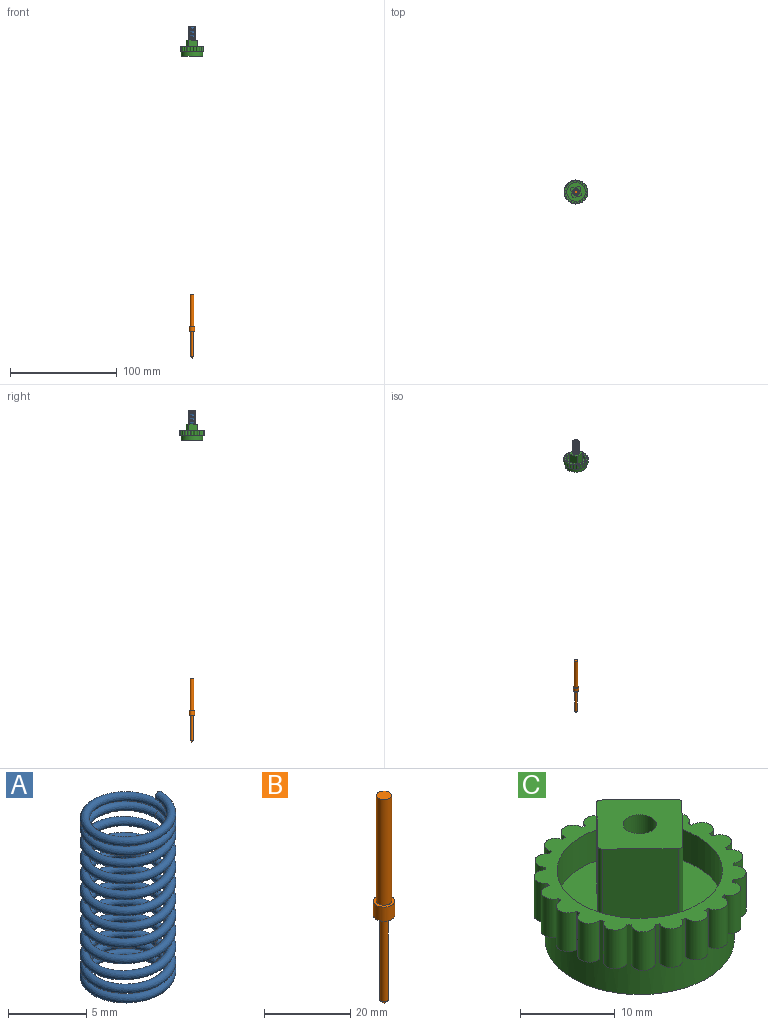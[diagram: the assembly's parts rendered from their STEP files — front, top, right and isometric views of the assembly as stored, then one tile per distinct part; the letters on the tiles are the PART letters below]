
ASSEMBLY  parts=3 mates=1
PART A: 5 faces, bbox 6.7x7.7x13.6 mm
  f0: plane 0.6x0.6mm, normal (0,1,0), area 0.3mm2, adj f1
  f1: bspline ~7.74x6.7mm, area 65.2mm2, adj f0,f2
  f2: bspline ~10.6x7.74mm, area 261.7mm2, adj f1,f4
  f3: plane 0.6x0.6mm, normal (0,-1,0), area 0.3mm2, adj f4
  f4: bspline ~7.74x6.7mm, area 65.2mm2, adj f2,f3
PART B: 7 faces, bbox 5x5x59 mm
  f0: cylinder r=2.5mm len=5mm, axis (0,0,1), area 62.8mm2, adj f3,f5
  f1: cylinder r=1mm len=24mm, axis (0,0,-1), area 150.8mm2, adj f2,f3
  f2: cone r=1mm half-angle=45deg, axis (0,0,1), area 4.4mm2, adj f1
  f3: plane 5x5mm, normal (0,0,-1), area 16.5mm2, adj f0,f1
  f4: cylinder r=1.75mm len=30mm, axis (0,0,1), area 329.9mm2, adj f5,f6
  f5: plane 5x5mm, normal (0,0,1), area 10mm2, adj f0,f4
  f6: plane 3.5x3.5mm, normal (0,0,1), area 9.6mm2, adj f4
PART C: 57 faces, bbox 22.4x22.4x15 mm
  f0: plane 17.5x17.5mm, normal (0,0,1), area 159.7mm2, adj f1,f2,f3,f4,f47,f53,f54,f55
  f1: plane 10x5.73mm, normal (0.72,-0.7,0), area 80mm2, adj f0,f5,f53,f56
  f2: plane 10x5.73mm, normal (0.7,0.72,0), area 80mm2, adj f0,f5,f53,f54
  f3: plane 10x5.73mm, normal (-0.72,0.7,0), area 80mm2, adj f0,f5,f54,f55
  f4: plane 10x5.73mm, normal (-0.7,-0.72,0), area 80mm2, adj f0,f5,f55,f56
  f5: plane 12.31x12.31mm, normal (0,0,1), area 71.2mm2, adj f1,f2,f3,f4,f52,f53,f54,f55
  f6: plane 2.44x1.78mm, normal (0,0,-1), area 2.5mm2, adj f43,f51
  f7: plane 2.27x2.09mm, normal (0,0,-1), area 2.5mm2, adj f44,f51
  f8: plane 2.32x2.02mm, normal (0,0,-1), area 2.5mm2, adj f45,f51
  f9: plane 2.47x1.69mm, normal (0,0,-1), area 2.5mm2, adj f46,f51
  f10: plane 2.5x1.33mm, normal (0,0,-1), area 2.5mm2, adj f26,f51
  f11: plane 2.47x1.69mm, normal (0,0,-1), area 2.5mm2, adj f27,f51
  f12: plane 2.32x2.02mm, normal (0,0,-1), area 2.5mm2, adj f28,f51
  f13: plane 2.27x2.09mm, normal (0,0,-1), area 2.5mm2, adj f29,f51
  f14: plane 2.44x1.78mm, normal (0,0,-1), area 2.5mm2, adj f30,f51
  f15: plane 2.5x1.42mm, normal (0,0,-1), area 2.5mm2, adj f31,f51
  f16: plane 2.48x1.6mm, normal (0,0,-1), area 2.5mm2, adj f32,f51
  f17: plane 2.37x1.94mm, normal (0,0,-1), area 2.5mm2, adj f33,f51
  f18: plane 2.22x2.16mm, normal (0,0,-1), area 2.5mm2, adj f34,f51
  f19: plane 2.41x1.86mm, normal (0,0,-1), area 2.5mm2, adj f35,f51
  f20: plane 2.5x1.51mm, normal (0,0,-1), area 2.5mm2, adj f36,f51
  f21: plane 2.5x1.51mm, normal (0,0,-1), area 2.5mm2, adj f37,f51
  f22: plane 2.41x1.86mm, normal (0,0,-1), area 2.5mm2, adj f38,f51
  f23: plane 2.22x2.16mm, normal (0,0,-1), area 2.5mm2, adj f39,f51
  f24: plane 2.37x1.94mm, normal (0,0,-1), area 2.5mm2, adj f40,f51
  f25: plane 2.48x1.6mm, normal (0,0,-1), area 2.5mm2, adj f41,f51
  f26: cylinder r=1.25mm len=5mm, axis (0,0,-1), area 20.4mm2, adj f10,f48,f51
  f27: cylinder r=1.25mm len=5mm, axis (0,0,-1), area 20.4mm2, adj f11,f48,f51
  f28: cylinder r=1.25mm len=5mm, axis (0,0,-1), area 20.4mm2, adj f12,f48,f51
  f29: cylinder r=1.25mm len=5mm, axis (0,0,-1), area 20.4mm2, adj f13,f48,f51
  f30: cylinder r=1.25mm len=5mm, axis (0,0,-1), area 20.4mm2, adj f14,f48,f51
  f31: cylinder r=1.25mm len=5mm, axis (0,0,-1), area 20.4mm2, adj f15,f48,f51
  f32: cylinder r=1.25mm len=5mm, axis (0,0,-1), area 20.4mm2, adj f16,f48,f51
  f33: cylinder r=1.25mm len=5mm, axis (0,0,-1), area 20.4mm2, adj f17,f48,f51
  f34: cylinder r=1.25mm len=5mm, axis (0,0,-1), area 20.4mm2, adj f18,f48,f51
  f35: cylinder r=1.25mm len=5mm, axis (0,0,-1), area 20.4mm2, adj f19,f48,f51
  f36: cylinder r=1.25mm len=5mm, axis (0,0,-1), area 20.4mm2, adj f20,f48,f51
  f37: cylinder r=1.25mm len=5mm, axis (0,0,-1), area 20.4mm2, adj f21,f48,f51
  f38: cylinder r=1.25mm len=5mm, axis (0,0,-1), area 20.4mm2, adj f22,f48,f51
  f39: cylinder r=1.25mm len=5mm, axis (0,0,-1), area 20.4mm2, adj f23,f48,f51
  f40: cylinder r=1.25mm len=5mm, axis (0,0,-1), area 20.4mm2, adj f24,f48,f51
  f41: cylinder r=1.25mm len=5mm, axis (0,0,-1), area 20.4mm2, adj f25,f48,f51
  f42: cylinder r=1.25mm len=5mm, axis (0,0,-1), area 20.4mm2, adj f48,f49,f51
  f43: cylinder r=1.25mm len=5mm, axis (0,0,-1), area 20.4mm2, adj f6,f48,f51
  f44: cylinder r=1.25mm len=5mm, axis (0,0,-1), area 20.4mm2, adj f7,f48,f51
  f45: cylinder r=1.25mm len=5mm, axis (0,0,-1), area 20.4mm2, adj f8,f48,f51
  f46: cylinder r=1.25mm len=5mm, axis (0,0,-1), area 20.4mm2, adj f9,f48,f51
  f47: cylinder r=8.75mm len=17.5mm, axis (0,0,-1), area 219.9mm2, adj f0,f48
  f48: plane 22.44x22.39mm, normal (0,0,1), area 126.5mm2, adj f26,f27,f28,f29,f30,f31,f32,f33
  f49: plane 2.5x1.42mm, normal (0,0,-1), area 2.5mm2, adj f42,f51
  f50: plane 20x20mm, normal (0,0,-1), area 304.5mm2, adj f51,f52
  f51: cylinder r=10mm len=20mm, axis (0,0,-1), area 302.8mm2, adj f6,f7,f8,f9,f10,f11,f12,f13
  f52: cylinder r=1.75mm len=15mm, axis (0,0,-1), area 164.9mm2, adj f5,f50
  f53: cylinder r=0.5mm len=10mm, axis (0,0,-1), area 7.9mm2, adj f0,f1,f2,f5
  f54: cylinder r=0.5mm len=10mm, axis (0,0,-1), area 7.9mm2, adj f0,f2,f3,f5
  f55: cylinder r=0.5mm len=10mm, axis (0,0,-1), area 7.9mm2, adj f0,f3,f4,f5
  f56: cylinder r=0.5mm len=10mm, axis (0,0,-1), area 7.9mm2, adj f0,f1,f4,f5
PLACE A rot(axis=(-0.29,-0.96,0),180deg) t=(0,0,297)mm
PLACE B at identity fixed
PLACE C rot(axis=(0,0,1),56.7deg) t=(0,0,282)mm
MATE cylindrical C.f51 <-> B.f0  axis (0,0,-1) through (0,0,282)mm
